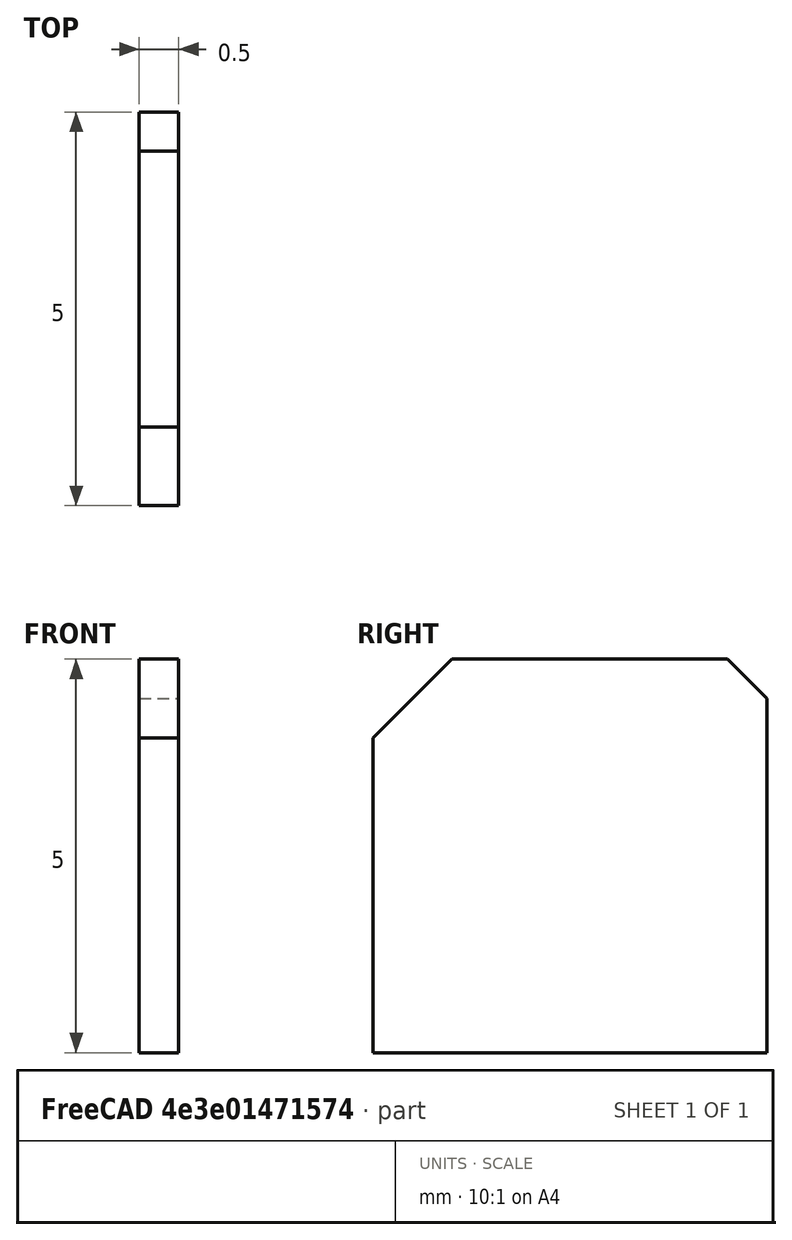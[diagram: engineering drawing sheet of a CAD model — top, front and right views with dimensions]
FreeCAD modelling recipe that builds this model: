
FCSTD DOCUMENT  (FreeCAD 1.1R20260108 (Git shallow))
Label: LiNbO3_Substrate_5mm
License: All rights reserved
LicenseURL: https://en.wikipedia.org/wiki/All_rights_reserved
objects: TechDraw::DrawViewDimension×6, TechDraw::DrawViewAnnotation×3, TechDraw::DrawProjGroupItem×2, App::Point×1, Sketcher::SketchObject×1, PartDesign::Pad×1, PartDesign::Body×1, TechDraw::DrawSVGTemplate×1, TechDraw::DrawProjGroup×1, TechDraw::DrawPage×1
note: 18 computed .brp shape members not serialized (recipe doc carries the construction recipe); baked Part::Feature solids carry a one-line shape summary decoded from their .brp

FEATURE [App::Point] Origin001
  Role = Origin
FEATURE [Sketcher::SketchObject] Sketch
  ArcFitTolerance = 1e-06
  AttachmentSupport = -> [Origin]
  ExternalTypes = [0]
  FullyConstrained = true
  MakeInternals = false
  MapMode = 5
  Placement = pos=(0,0,0) rot=(0.57735,0.57735,0.57735;2.0944rad)
  sketch-geometry (10):
    g0: LineSegment [constr] StartX=-2.5 StartY=-2.5 StartZ=0 EndX=2.5 EndY=-2.5 EndZ=0
    g1: LineSegment [constr] StartX=2.5 StartY=-2.5 StartZ=0 EndX=2.5 EndY=2.5 EndZ=0
    g2: LineSegment [constr] StartX=2.5 StartY=2.5 StartZ=0 EndX=-2.5 EndY=2.5 EndZ=0
    g3: LineSegment [constr] StartX=-2.5 StartY=2.5 StartZ=0 EndX=-2.5 EndY=-2.5 EndZ=0
    g4: LineSegment StartX=-2.5 StartY=-2.5 StartZ=0 EndX=2.5 EndY=-2.5 EndZ=0
    g5: LineSegment StartX=2.5 StartY=-2.5 StartZ=0 EndX=2.5 EndY=2 EndZ=0
    g6: LineSegment StartX=-2.5 StartY=-2.5 StartZ=0 EndX=-2.5 EndY=1.5 EndZ=0
    g7: LineSegment StartX=-1.5 StartY=2.5 StartZ=0 EndX=2 EndY=2.5 EndZ=0
    g8: LineSegment StartX=-1.5 StartY=2.5 StartZ=0 EndX=-2.5 EndY=1.5 EndZ=0
    g9: LineSegment StartX=2 StartY=2.5 StartZ=0 EndX=2.5 EndY=2 EndZ=0
  constraints (28):
    c: Coincident(g0,g1)
    c: Coincident(g1,g2)
    c: Coincident(g2,g3)
    c: Coincident(g3,g0)
    c: Horizontal(g0)
    c: Horizontal(g2)
    c: Vertical(g1)
    c: Vertical(g3)
    c: Equal(g3,g2)
    c: Distance(g2,g2) = 5
    c: DistanceX(g-2,g2) = -2.5
    c: DistanceY(g-1,g0) = -2.5
    c: Coincident(g4,g0)
    c: Coincident(g4,g0)
    c: Coincident(g5,g0)
    c: PointOnObject(g5,g1)
    c: Coincident(g6,g0)
    c: PointOnObject(g6,g3)
    c: PointOnObject(g7,g2)
    c: PointOnObject(g7,g2)
    c: Coincident(g8,g7)
    c: Coincident(g8,g6)
    c: Coincident(g9,g7)
    c: Coincident(g9,g5)
    c: Distance(g6,g2) = 1
    c: Distance(g2,g7) = 1
    c: Distance(g5,g1) = 0.5
    c: Distance(g1,g7) = 0.5
FEATURE [PartDesign::Pad] Pad
  Direction = (1,0,0)
  Length = 0.5
  Length2 = 10
  Profile = -> Sketch
  ReferenceAxis = -> Sketch [N_Axis]
  Refine = true
  SideType = 0
  Suppressed = false
  Type = 0
  Type2 = 0
FEATURE [PartDesign::Body] Body
  AllowCompound = false
  Group = -> [Sketch,Pad]
  Origin = -> Origin
  Tip = -> Pad
FEATURE [TechDraw::DrawSVGTemplate] Template
  Height = 210
  Orientation = 1
  Template = /Applications/FreeCAD.app/Contents/Resources/share/Mod/TechDraw/Templates/ISO/A4_Landscape_TD.svg
  Width = 297
FEATURE [TechDraw::DrawProjGroupItem] ProjItem  label="Front"
  CoarseView = false
  Direction = (1,0,0)
  Focus = 100
  HardHidden = true
  IsoCount = 0
  IsoHidden = false
  IsoVisible = false
  LockPosition = true
  Perspective = false
  Rotation = 0
  RotationVector = (0,1,0)
  Scale = 10
  ScaleType = 2
  ScrubCount = 1
  SeamHidden = false
  SeamVisible = false
  SmoothHidden = false
  SmoothVisible = true
  Source = -> [Body]
  Type = 0
  X = 0
  XDirection = (0,1,0)
  Y = 0
FEATURE [TechDraw::DrawProjGroupItem] ProjItem001  label="FrontTopRight"
  CoarseView = false
  Direction = (0.57735,0.57735,0.57735)
  Focus = 100
  HardHidden = true
  IsoCount = 0
  IsoHidden = false
  IsoVisible = false
  LockPosition = false
  Perspective = false
  Rotation = 0
  RotationVector = (1,0,0)
  Scale = 10
  ScaleType = 2
  ScrubCount = 1
  SeamHidden = false
  SeamVisible = false
  SmoothHidden = false
  SmoothVisible = true
  Source = -> [Body]
  Type = 7
  X = -59.4454
  XDirection = (-0.707107,0.707107,0)
  Y = -69.598
FEATURE [TechDraw::DrawProjGroup] ProjGroup
  Anchor = -> ProjItem
  AutoDistribute = true
  LockPosition = false
  ProjectionType = 0
  Rotation = 0
  Scale = 10
  ScaleType = 2
  Source = -> [Body]
  Views = -> [ProjItem,ProjItem001]
  X = 148.077
  Y = 134.929
  spacingX = 15
  spacingY = 15
FEATURE [TechDraw::DrawViewDimension] Dimension
  AngleOverride = false
  Arbitrary = false
  ArbitraryTolerances = false
  BoxCorners = (2) [(-25,-25,0),(25,25,0)]
  EqualTolerance = true
  ExtensionAngle = 0
  FormatSpec = %.2w
  FormatSpecOverTolerance = %+.2w
  FormatSpecUnderTolerance = %+.2w
  Inverted = false
  LineAngle = 0
  LockPosition = false
  MeasureType = 1
  OverTolerance = 0
  References2D = -> [ProjItem]
  Rotation = 0
  ScaleType = 0
  ShowUnits = false
  TheoreticalExact = false
  Type = 1
  UnderTolerance = 0
  UseActualArea = true
  X = -5.41575
  Y = -12.2703
FEATURE [TechDraw::DrawViewDimension] Dimension001
  AngleOverride = false
  Arbitrary = false
  ArbitraryTolerances = false
  BoxCorners = (2) [(-25,-25,0),(25,25,0)]
  EqualTolerance = true
  ExtensionAngle = 0
  FormatSpec = %.2w
  FormatSpecOverTolerance = %+.2w
  FormatSpecUnderTolerance = %+.2w
  Inverted = false
  LineAngle = 0
  LockPosition = false
  MeasureType = 1
  OverTolerance = 0
  References2D = -> [ProjItem]
  Rotation = 0
  ScaleType = 0
  ShowUnits = false
  TheoreticalExact = false
  Type = 2
  UnderTolerance = 0
  UseActualArea = true
  X = 9.26151
  Y = 4.51312
FEATURE [TechDraw::DrawViewDimension] Dimension002
  AngleOverride = false
  Arbitrary = false
  ArbitraryTolerances = false
  BoxCorners = (2) [(-25,-25,0),(25,25,0)]
  EqualTolerance = true
  ExtensionAngle = 0
  FormatSpec = %.2w
  FormatSpecOverTolerance = %+.2w
  FormatSpecUnderTolerance = %+.2w
  Inverted = false
  LineAngle = 0
  LockPosition = false
  MeasureType = 1
  OverTolerance = 0.1
  References2D = -> [ProjItem]
  Rotation = 0
  ScaleType = 0
  ShowUnits = false
  TheoreticalExact = false
  Type = 2
  UnderTolerance = -0.1
  UseActualArea = true
  X = 35.4748
  Y = 5.37843
FEATURE [TechDraw::DrawViewDimension] Dimension003
  AngleOverride = false
  Arbitrary = false
  ArbitraryTolerances = false
  BoxCorners = (2) [(-25,-25,0),(25,25,0)]
  EqualTolerance = true
  ExtensionAngle = 0
  FormatSpec = %.2w
  FormatSpecOverTolerance = %+.2w
  FormatSpecUnderTolerance = %+.2w
  Inverted = false
  LineAngle = 0
  LockPosition = false
  MeasureType = 1
  OverTolerance = 0.1
  References2D = -> [ProjItem]
  Rotation = 0
  ScaleType = 0
  ShowUnits = false
  TheoreticalExact = false
  Type = 1
  UnderTolerance = -0.1
  UseActualArea = true
  X = 37.996
  Y = 41.3764
FEATURE [TechDraw::DrawViewDimension] Dimension004
  AngleOverride = false
  Arbitrary = false
  ArbitraryTolerances = false
  BoxCorners = (2) [(-25,-25,0),(25,25,0)]
  EqualTolerance = true
  ExtensionAngle = 0
  FormatSpec = %.2w
  FormatSpecOverTolerance = %+.2w
  FormatSpecUnderTolerance = %+.2w
  Inverted = false
  LineAngle = 0
  LockPosition = false
  MeasureType = 1
  OverTolerance = 0.1
  References2D = -> [ProjItem]
  Rotation = 0
  ScaleType = 0
  ShowUnits = false
  TheoreticalExact = false
  Type = 2
  UnderTolerance = -0.1
  UseActualArea = true
  X = -38.51
  Y = -5.67511
FEATURE [TechDraw::DrawViewDimension] Dimension005
  AngleOverride = false
  Arbitrary = false
  ArbitraryTolerances = false
  BoxCorners = (2) [(-25,-25,0),(25,25,0)]
  EqualTolerance = true
  ExtensionAngle = 0
  FormatSpec = %.2w
  FormatSpecOverTolerance = %+.2w
  FormatSpecUnderTolerance = %+.2w
  Inverted = false
  LineAngle = 0
  LockPosition = false
  MeasureType = 1
  OverTolerance = 0.1
  References2D = -> [ProjItem]
  Rotation = 0
  ScaleType = 0
  ShowUnits = false
  TheoreticalExact = false
  Type = 1
  UnderTolerance = -0.1
  UseActualArea = true
  X = -40.6993
  Y = 41.3764
FEATURE [TechDraw::DrawViewAnnotation] Annotation
  Font = osifont
  LineSpace = 100
  LockPosition = false
  MaxWidth = -1
  Rotation = 0
  ScaleType = 0
  Text = +X
  TextSize = 5
  TextStyle = 0
  X = 52.7028
  Y = 48.7595
FEATURE [TechDraw::DrawViewAnnotation] Annotation001
  Font = osifont
  LineSpace = 100
  LockPosition = false
  MaxWidth = -1
  Rotation = 0
  ScaleType = 0
  Text = +Y
  TextSize = 5
  TextStyle = 0
  X = 123.408
  Y = 46.4322
FEATURE [TechDraw::DrawViewAnnotation] Annotation002
  Font = osifont
  LineSpace = 100
  LockPosition = false
  MaxWidth = -1
  Rotation = 0
  ScaleType = 0
  Text = +Z
  TextSize = 5
  TextStyle = 0
  X = 88.6318
  Y = 105.71
FEATURE [TechDraw::DrawPage] Page
  KeepUpdated = true
  NextBalloonIndex = 1
  ProjectionType = 0
  Template = -> Template
  Views = -> [ProjGroup,Dimension,Dimension001,Dimension002,Dimension003,Dimension004,Dimension005,Annotation,Annotation001,Annotation002]
